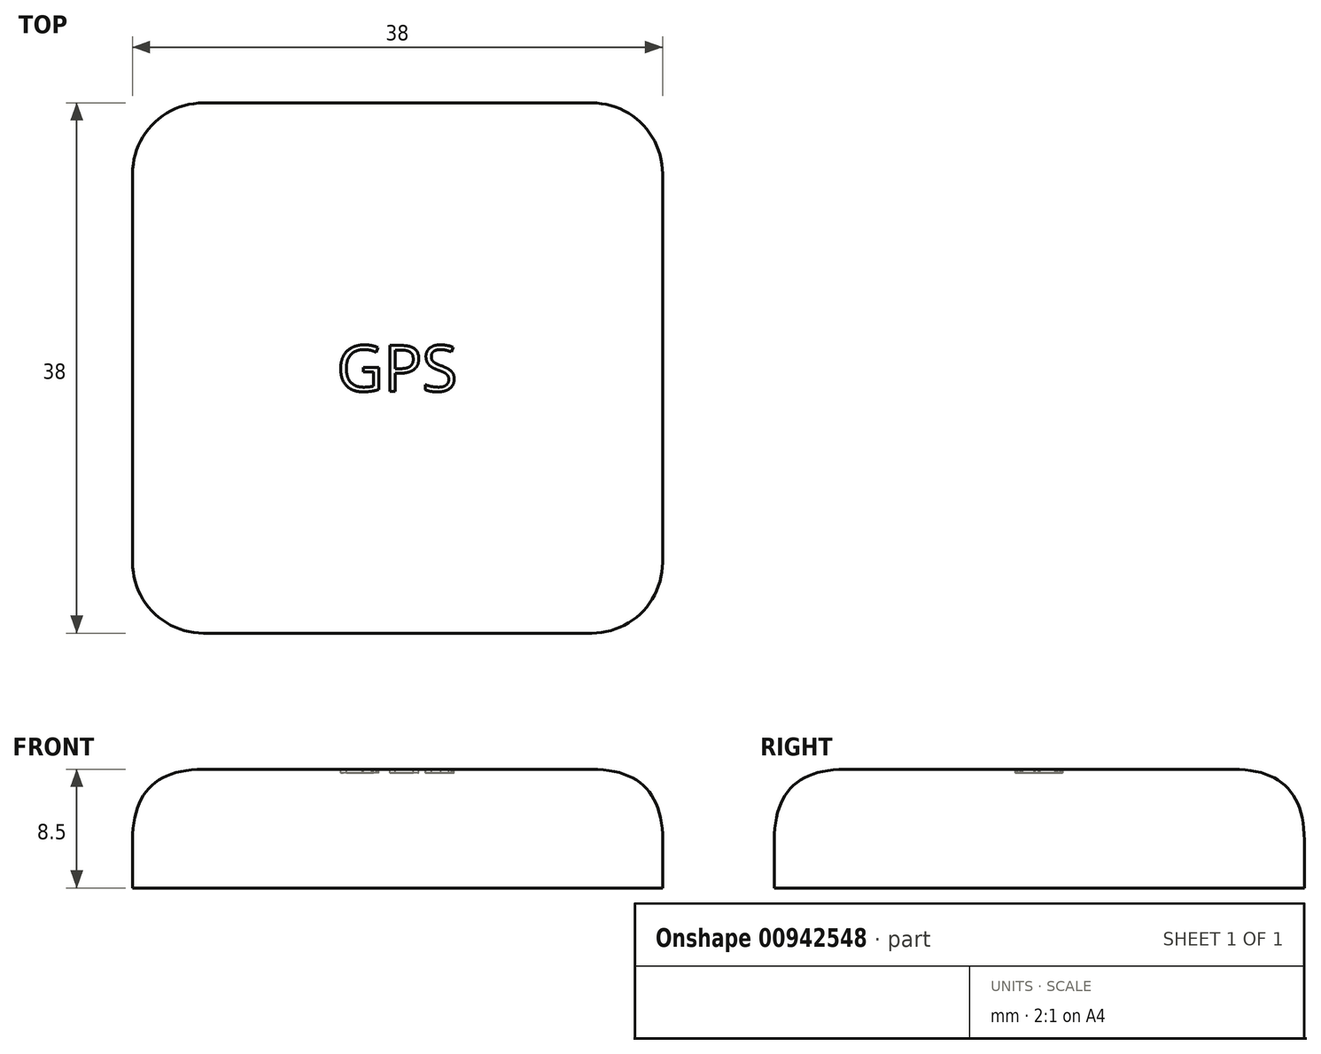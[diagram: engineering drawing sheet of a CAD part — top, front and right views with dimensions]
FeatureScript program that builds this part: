
annotation { "Feature Type Name" : "Feature", "Feature Type Description" : "" }
export const myFeature = defineFeature(function(context is Context, id is Id, definition is map)
    precondition{}
    {
        {
            var Q0;
            Q0=qCreatedBy(makeId("Top.planeOp"),FACE);
            var sketch = newSketch(context, id + "F0", { "sketchPlane" : qUnion([Q0])});
            skLineSegment(sketch, "E0.bottom", {"start": v(19, 19) * mm, "end": v(-19, 19) * mm});
            skLineSegment(sketch, "E0.top", {"start": v(19, -19) * mm, "end": v(-19, -19) * mm});
            skLineSegment(sketch, "E0.left", {"start": v(19, 19) * mm, "end": v(19, -19) * mm});
            skLineSegment(sketch, "E0.right", {"start": v(-19, 19) * mm, "end": v(-19, -19) * mm});
            skPoint(sketch, "E0.middle", {"position": v(0, 0) * mm});
            skSolve(sketch);
        }
        {
            var Q0;
            Q0=makeQuery(id+"F0.imprint","IMPRINT",FACE,{"disambiguationData":[TD([[makeQuery(id+"F0.imprint","IMPRINT",EDGE,{"derivedFrom":sQuery(id+"F0.wireOp",EDGE,"E0.bottom")}),1.0]])]});
            extrude(context, id + "F1", {"entities" : qUnion([Q0]), "depth" : 8.5 * mm, "offsetDistance" : 25.4 * mm});
        }
        {
            var Q0;
            Q0=makeQuery(id+"F1.opExtrude","CAP_FACE",FACE,{"disambiguationData":[OSD([sQuery(id+"F0.wireOp",EDGE,"E0.bottom"),sQuery(id+"F0.wireOp",EDGE,"E0.top"),sQuery(id+"F0.wireOp",EDGE,"E0.left"),sQuery(id+"F0.wireOp",EDGE,"E0.right")])],"isStart":false});
            var sketch = newSketch(context, id + "F2", { "sketchPlane" : qUnion([Q0])});
            skText(sketch, "E1", { "text": "GPS\n", "fontName": "OpenSans-Regular.ttf"});
            skPoint(sketch, "E2", {"position": v(4.36, 0) * mm});
            const initialGuessF2  = {"E1": [-0.00436, -0.00166, 1, 0, 0.00331]};
            skSetInitialGuess(sketch, initialGuessF2);
            skSolve(sketch);
        }
        {
            var Q0;
            Q0 = qSketchRegion(id + "F2", true);
            extrude(context, id + "F3", {"entities" : qUnion([Q0]), "operationType" : NewBodyOperationType.REMOVE, "oppositeDirection" : true, "depth" : 0.25 * mm, "offsetDistance" : 25.4 * mm});
        }
        {
            var Q0;
            Q0=makeQuery(id+"F1.opExtrude","SWEPT_EDGE",EDGE,{"disambiguationData":[OSD([sQuery(id+"F0.wireOp",EDGE,"E0.top"),sQuery(id+"F0.wireOp",EDGE,"E0.right")])]});
            var Q1;
            Q1=makeQuery(id+"F1.opExtrude","SWEPT_EDGE",EDGE,{"disambiguationData":[OSD([sQuery(id+"F0.wireOp",EDGE,"E0.top"),sQuery(id+"F0.wireOp",EDGE,"E0.left")])]});
            var Q2;
            Q2=makeQuery(id+"F1.opExtrude","SWEPT_EDGE",EDGE,{"disambiguationData":[OSD([sQuery(id+"F0.wireOp",EDGE,"E0.bottom"),sQuery(id+"F0.wireOp",EDGE,"E0.left")])]});
            var Q3;
            Q3=makeQuery(id+"F1.opExtrude","SWEPT_EDGE",EDGE,{"disambiguationData":[OSD([sQuery(id+"F0.wireOp",EDGE,"E0.bottom"),sQuery(id+"F0.wireOp",EDGE,"E0.right")])]});
            fillet(context, id + "F4", {"entities" : qUnion([Q0, Q1, Q2, Q3]), "radius" : 5.08 * mm, "tangentPropagation" : true, "allowEdgeOverflow" : false});
        }
        {
            var Q0;
            Q0=makeQuery(id+"F1.opExtrude","CAP_EDGE",EDGE,{"disambiguationData":[OSD([sQuery(id+"F0.wireOp",EDGE,"E0.top")])],"isStart":false});
            fillet(context, id + "F5", {"entities" : qUnion([Q0]), "radius" : 5.08 * mm, "tangentPropagation" : true, "rho" : 0.5, "crossSection" : FilletCrossSection.CONIC, "allowEdgeOverflow" : false});
        }
    });
